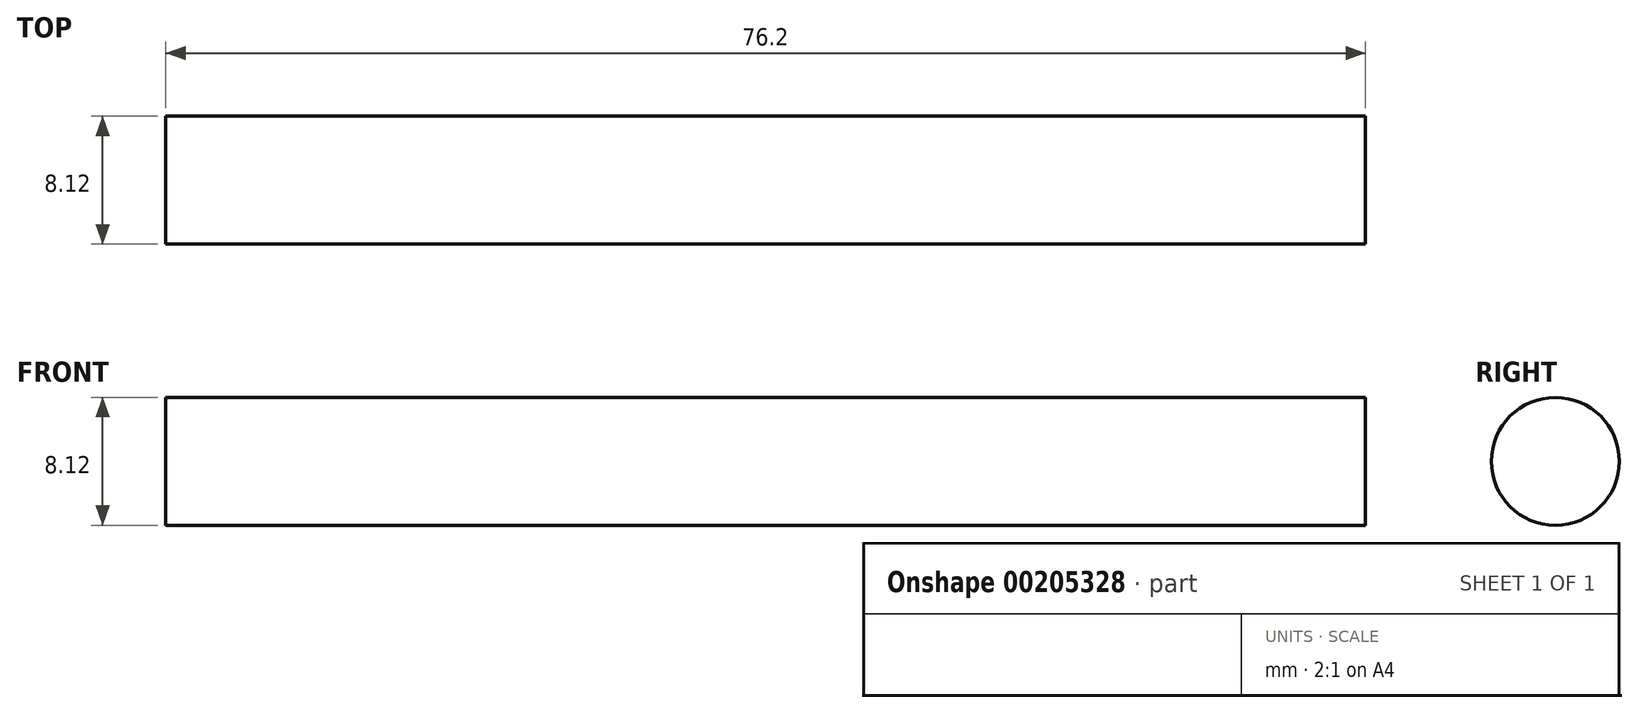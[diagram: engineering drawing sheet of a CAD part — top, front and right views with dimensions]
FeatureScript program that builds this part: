
annotation { "Feature Type Name" : "Feature", "Feature Type Description" : "" }
export const myFeature = defineFeature(function(context is Context, id is Id, definition is map)
    precondition{}
    {
        {
            var Q0;
            Q0=qCreatedBy(makeId("Right.planeOp"),FACE);
            var sketch = newSketch(context, id + "F0", { "sketchPlane" : qUnion([Q0])});
            skCircle(sketch, "E0", {"center": v(0, 0) * mm, "radius": 4.06 * mm});
            skSolve(sketch);
        }
        {
            var Q0;
            Q0=sQuery(id+"F0.wireOp",EDGE,"E0");
            extrude(context, id + "F1", {"bodyType" : ToolBodyType.SURFACE, "surfaceEntities" : qUnion([Q0]), "depth" : 76.2 * mm});
        }
    });
